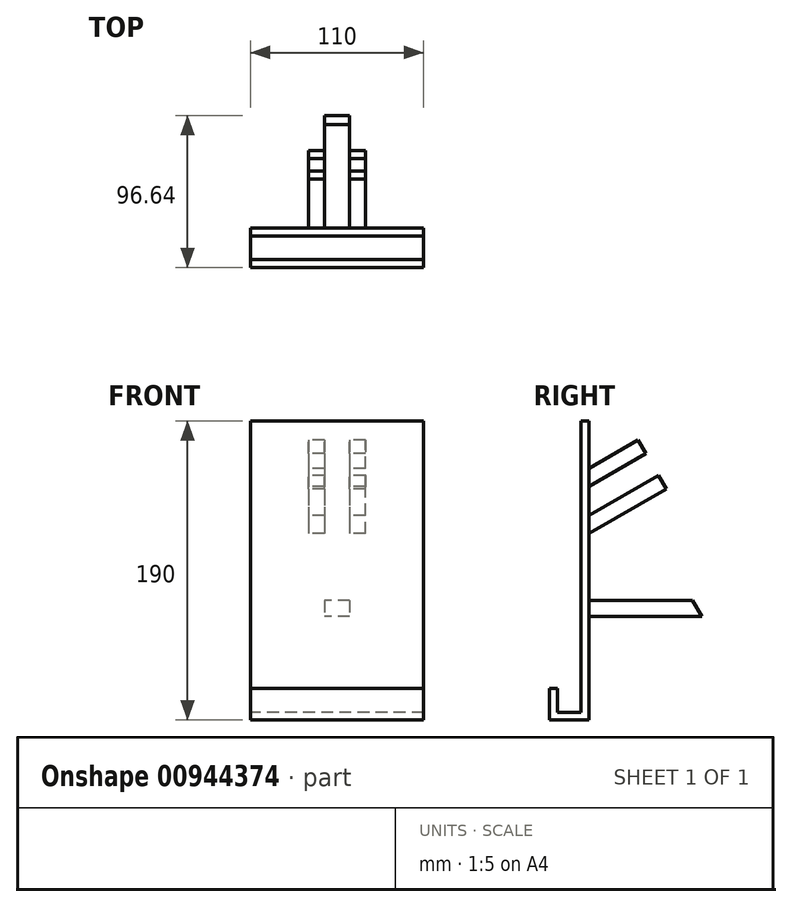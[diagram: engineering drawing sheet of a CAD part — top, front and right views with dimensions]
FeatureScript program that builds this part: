
annotation { "Feature Type Name" : "Feature", "Feature Type Description" : "" }
export const myFeature = defineFeature(function(context is Context, id is Id, definition is map)
    precondition{}
    {
        {
            var Q0;
            Q0=qCreatedBy(makeId("Right.planeOp"),FACE);
            var sketch = newSketch(context, id + "F0", { "sketchPlane" : qUnion([Q0])});
            skLineSegment(sketch, "E0.bottom", {"start": v(-5, 114.09) * mm, "end": v(0, 114.09) * mm});
            skLineSegment(sketch, "E0.top", {"start": v(-5, -75.91) * mm, "end": v(0, -75.91) * mm});
            skLineSegment(sketch, "E0.left", {"start": v(-5, 114.09) * mm, "end": v(-5, -75.91) * mm});
            skLineSegment(sketch, "E0.right", {"start": v(0, 114.09) * mm, "end": v(0, -75.91) * mm});
            skLineSegment(sketch, "E1.bottom", {"start": v(-5, -75.91) * mm, "end": v(-20, -75.91) * mm});
            skLineSegment(sketch, "E1.top", {"start": v(-5, -70.91) * mm, "end": v(-20, -70.91) * mm});
            skLineSegment(sketch, "E1.left", {"start": v(-5, -75.91) * mm, "end": v(-5, -70.91) * mm});
            skLineSegment(sketch, "E1.right", {"start": v(-20, -75.91) * mm, "end": v(-20, -70.91) * mm});
            skLineSegment(sketch, "E2.bottom", {"start": v(-25, -75.91) * mm, "end": v(-20, -75.91) * mm});
            skLineSegment(sketch, "E2.top", {"start": v(-25, -55.91) * mm, "end": v(-20, -55.91) * mm});
            skLineSegment(sketch, "E2.left", {"start": v(-25, -75.91) * mm, "end": v(-25, -55.91) * mm});
            skLineSegment(sketch, "E2.right", {"start": v(-20, -75.91) * mm, "end": v(-20, -55.91) * mm});
            skLineSegment(sketch, "E3.bottom", {"start": v(0, 84.09) * mm, "end": v(31.15, 102.07) * mm});
            skLineSegment(sketch, "E3.top", {"start": v(0, 72.54) * mm, "end": v(36.15, 93.41) * mm});
            skLineSegment(sketch, "E3.right", {"start": v(31.15, 102.07) * mm, "end": v(36.15, 93.41) * mm});
            skLineSegment(sketch, "E4.bottom", {"start": v(0, 54.07) * mm, "end": v(44.15, 79.56) * mm});
            skLineSegment(sketch, "E4.top", {"start": v(0, 42.52) * mm, "end": v(49.15, 70.9) * mm});
            skLineSegment(sketch, "E4.right", {"start": v(44.15, 79.56) * mm, "end": v(49.15, 70.9) * mm});
            skLineSegment(sketch, "E5.bottom", {"start": v(0, 0) * mm, "end": v(65.87, 0) * mm});
            skLineSegment(sketch, "E5.top", {"start": v(0, -10) * mm, "end": v(71.64, -10) * mm});
            skLineSegment(sketch, "E5.left", {"start": v(0, 0) * mm, "end": v(0, -10) * mm});
            skLineSegment(sketch, "E6", {"start": v(71.64, -10) * mm, "end": v(71.64, -10) * mm});
            skLineSegment(sketch, "E7", {"start": v(71.64, -10) * mm, "end": v(65.87, 0) * mm});
            skLineSegment(sketch, "E8", {"start": v(0, 114.09) * mm, "end": v(71.64, -10) * mm});
            skSolve(sketch);
        }
        {
            var Q0;
            {var subQ0=sQuery(id+"F0.wireOp",EDGE,"E4.right");var subQ1=sQuery(id+"F0.wireOp",EDGE,"E4.bottom");var subQ7=sQuery(id+"F0.wireOp",EDGE,"E0.right");var subQ8=makeQuery(id+"F0.imprint","INTERSECT",VERTEX,{"derivedFrom":[subQ7,subQ1]});Q0=qUnion([makeQuery(id+"F0.imprint","IMPRINT",FACE,{"disambiguationData":[TD([[makeQuery(id+"F0.imprint","IMPRINT",EDGE,{"disambiguationData":[TD([[subQ8,-1.0]])],"derivedFrom":subQ7}),1.0]])]}),makeQuery(id+"F0.imprint","IMPRINT",FACE,{"disambiguationData":[TD([[makeQuery(id+"F0.imprint","IMPRINT",EDGE,{"derivedFrom":subQ0}),-1.0]])]})]);}
            var Q1;
            {var subQ1=sQuery(id+"F0.wireOp",EDGE,"E3.bottom");var subQ3=sQuery(id+"F0.wireOp",EDGE,"E3.right");var subQ7=sQuery(id+"F0.wireOp",EDGE,"E0.right");var subQ8=makeQuery(id+"F0.imprint","INTERSECT",VERTEX,{"derivedFrom":[subQ7,subQ1]});Q1=qUnion([makeQuery(id+"F0.imprint","IMPRINT",FACE,{"disambiguationData":[TD([[makeQuery(id+"F0.imprint","IMPRINT",EDGE,{"disambiguationData":[TD([[subQ8,-1.0]])],"derivedFrom":subQ7}),1.0]])]}),makeQuery(id+"F0.imprint","IMPRINT",FACE,{"disambiguationData":[TD([[makeQuery(id+"F0.imprint","IMPRINT",EDGE,{"derivedFrom":subQ3}),-1.0]])]})]);}
            var Q2;
            Q2=makeQuery(id+"F0.imprint","IMPRINT",FACE,{"disambiguationData":[TD([[makeQuery(id+"F0.imprint","IMPRINT",EDGE,{"derivedFrom":sQuery(id+"F0.wireOp",EDGE,"E1.right")}),1.0]])]});
            var Q3;
            {var subQ0=sQuery(id+"F0.wireOp",EDGE,"E1.bottom");Q3=makeQuery(id+"F0.imprint","IMPRINT",FACE,{"disambiguationData":[TD([[makeQuery(id+"F0.imprint","IMPRINT",EDGE,{"derivedFrom":subQ0}),-1.0]])]});}
            var Q4;
            {var subQ5=sQuery(id+"F0.wireOp",EDGE,"E0.bottom");Q4=makeQuery(id+"F0.imprint","IMPRINT",FACE,{"disambiguationData":[TD([[makeQuery(id+"F0.imprint","IMPRINT",EDGE,{"derivedFrom":subQ5}),-1.0]])]});}
            var Q5;
            {var subQ2=sQuery(id+"F0.wireOp",EDGE,"E5.bottom");Q5=makeQuery(id+"F0.imprint","IMPRINT",FACE,{"disambiguationData":[TD([[makeQuery(id+"F0.imprint","IMPRINT",EDGE,{"derivedFrom":subQ2}),-1.0]])]});}
            extrude(context, id + "F1", {"entities" : qUnion([Q0, Q1, Q2, Q3, Q4, Q5]), "depth" : 110 * mm, "offsetDistance" : 25 * mm});
        }
        {
            var Q0;
            Q0=qCreatedBy(makeId("Front.planeOp"),FACE);
            var sketch = newSketch(context, id + "F2", { "sketchPlane" : qUnion([Q0])});
            skLineSegment(sketch, "E9.bottom", {"start": v(110, 114.11) * mm, "end": v(0, 114.11) * mm});
            skLineSegment(sketch, "E9.top", {"start": v(110, -75.89) * mm, "end": v(0, -75.89) * mm});
            skLineSegment(sketch, "E9.left", {"start": v(110, 114.11) * mm, "end": v(110, -75.89) * mm});
            skLineSegment(sketch, "E9.right", {"start": v(0, 114.11) * mm, "end": v(0, -75.89) * mm});
            skLineSegment(sketch, "E10", {"start": v(55, 114.11) * mm, "end": v(55, -75.89) * mm});
            skLineSegment(sketch, "E11", {"start": v(47, 114.11) * mm, "end": v(47, -75.89) * mm});
            skLineSegment(sketch, "E12", {"start": v(63, 114.11) * mm, "end": v(63, -75.89) * mm});
            skLineSegment(sketch, "E13", {"start": v(110, 15.28) * mm, "end": v(0, 15.28) * mm});
            skLineSegment(sketch, "E14", {"start": v(37, 114.11) * mm, "end": v(37, -75.89) * mm});
            skLineSegment(sketch, "E15", {"start": v(37, -75.89) * mm, "end": v(73, -75.89) * mm});
            skLineSegment(sketch, "E16", {"start": v(73, -75.89) * mm, "end": v(73, 114.11) * mm});
            skSolve(sketch);
        }
        {
            var Q0;
            {var subQ0=sQuery(id+"F2.wireOp",EDGE,"E11");var subQ1=sQuery(id+"F2.wireOp",EDGE,"E9.bottom");var subQ2=makeQuery(id+"F2.imprint","INTERSECT",VERTEX,{"derivedFrom":[subQ1,subQ0]});Q0=makeQuery(id+"F2.imprint","IMPRINT",FACE,{"disambiguationData":[TD([[makeQuery(id+"F2.imprint","IMPRINT",EDGE,{"disambiguationData":[TD([[subQ2,1.0]])],"derivedFrom":subQ1}),1.0]])]});}
            var Q1;
            {var subQ0=sQuery(id+"F2.wireOp",EDGE,"E10");var subQ1=sQuery(id+"F2.wireOp",EDGE,"E9.bottom");var subQ2=makeQuery(id+"F2.imprint","INTERSECT",VERTEX,{"derivedFrom":[subQ1,subQ0]});Q1=makeQuery(id+"F2.imprint","IMPRINT",FACE,{"disambiguationData":[TD([[makeQuery(id+"F2.imprint","IMPRINT",EDGE,{"disambiguationData":[TD([[subQ2,1.0]])],"derivedFrom":subQ1}),1.0]])]});}
            var Q2;
            {var subQ0=sQuery(id+"F2.wireOp",EDGE,"E9.left");var subQ1=sQuery(id+"F2.wireOp",EDGE,"E9.top");var subQ2=makeQuery(id+"F2.imprint","INTERSECT",VERTEX,{"derivedFrom":[subQ1,subQ0]});Q2=makeQuery(id+"F2.imprint","IMPRINT",FACE,{"disambiguationData":[TD([[makeQuery(id+"F2.imprint","IMPRINT",EDGE,{"disambiguationData":[TD([[subQ2,-1.0]])],"derivedFrom":subQ1}),-1.0]])]});}
            var Q3;
            {var subQ0=sQuery(id+"F2.wireOp",EDGE,"E9.right");var subQ1=sQuery(id+"F2.wireOp",EDGE,"E9.top");var subQ2=makeQuery(id+"F2.imprint","INTERSECT",VERTEX,{"derivedFrom":[subQ1,subQ0]});Q3=makeQuery(id+"F2.imprint","IMPRINT",FACE,{"disambiguationData":[TD([[makeQuery(id+"F2.imprint","IMPRINT",EDGE,{"disambiguationData":[TD([[subQ2,1.0]])],"derivedFrom":subQ1}),-1.0]])]});}
            var Q4;
            {var subQ0=sQuery(id+"F2.wireOp",EDGE,"E11");var subQ1=sQuery(id+"F2.wireOp",EDGE,"E9.top");var subQ2=makeQuery(id+"F2.imprint","INTERSECT",VERTEX,{"derivedFrom":[subQ1,subQ0]});Q4=makeQuery(id+"F2.imprint","IMPRINT",FACE,{"disambiguationData":[TD([[makeQuery(id+"F2.imprint","IMPRINT",EDGE,{"disambiguationData":[TD([[subQ2,-1.0]])],"derivedFrom":subQ1}),-1.0]])]});}
            var Q5;
            {var subQ0=sQuery(id+"F2.wireOp",EDGE,"E12");var subQ1=sQuery(id+"F2.wireOp",EDGE,"E9.top");var subQ2=makeQuery(id+"F2.imprint","INTERSECT",VERTEX,{"derivedFrom":[subQ1,subQ0]});Q5=makeQuery(id+"F2.imprint","IMPRINT",FACE,{"disambiguationData":[TD([[makeQuery(id+"F2.imprint","IMPRINT",EDGE,{"disambiguationData":[TD([[subQ2,1.0]])],"derivedFrom":subQ1}),-1.0]])]});}
            var Q6;
            {var subQ0=sQuery(id+"F2.wireOp",EDGE,"E9.left");var subQ1=sQuery(id+"F2.wireOp",EDGE,"E9.bottom");var subQ2=makeQuery(id+"F2.imprint","INTERSECT",VERTEX,{"derivedFrom":[subQ1,subQ0]});Q6=makeQuery(id+"F2.imprint","IMPRINT",FACE,{"disambiguationData":[TD([[makeQuery(id+"F2.imprint","IMPRINT",EDGE,{"disambiguationData":[TD([[subQ2,-1.0]])],"derivedFrom":subQ1}),1.0]])]});}
            var Q7;
            {var subQ0=sQuery(id+"F2.wireOp",EDGE,"E14");var subQ1=sQuery(id+"F2.wireOp",EDGE,"E9.bottom");var subQ2=makeQuery(id+"F2.imprint","INTERSECT",VERTEX,{"derivedFrom":[subQ1,subQ0]});Q7=makeQuery(id+"F2.imprint","IMPRINT",FACE,{"disambiguationData":[TD([[makeQuery(id+"F2.imprint","IMPRINT",EDGE,{"disambiguationData":[TD([[subQ2,-1.0]])],"derivedFrom":subQ1}),1.0]])]});}
            extrude(context, id + "F3", {"entities" : qUnion([Q0, Q1, Q2, Q3, Q4, Q5, Q6, Q7]), "operationType" : NewBodyOperationType.REMOVE, "oppositeDirection" : true, "depth" : 100 * mm, "offsetDistance" : 25 * mm});
        }
    });
